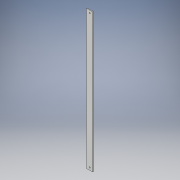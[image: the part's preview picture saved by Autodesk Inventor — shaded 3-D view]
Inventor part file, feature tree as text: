
AUTODESK INVENTOR PART (.ipt)
format: ipt  version: 2018 (Build 220112000, 112)  size: 100,864 bytes
history: native  units: in
note: dims shown in document units (in); Inventor stores cm internally (conversion verified against a paired STEP export)
features: extrude x1, sketch x1
ambient origin geometry x8: Origin, YZ Plane, XZ Plane, XY Plane, X Axis, Y Axis, Z Axis, Center Point
bodies: Solid1 (feature_tree)
feature tree (2):
  extrude  "Extrusion1"  Depth=23.0in
  sketch  "Sketch1"  dims[d0=1.0in d1=23.0in d2=0.4145in d3=0.2031in d4=0.4145in d5=0.125in d6=0.0in]
